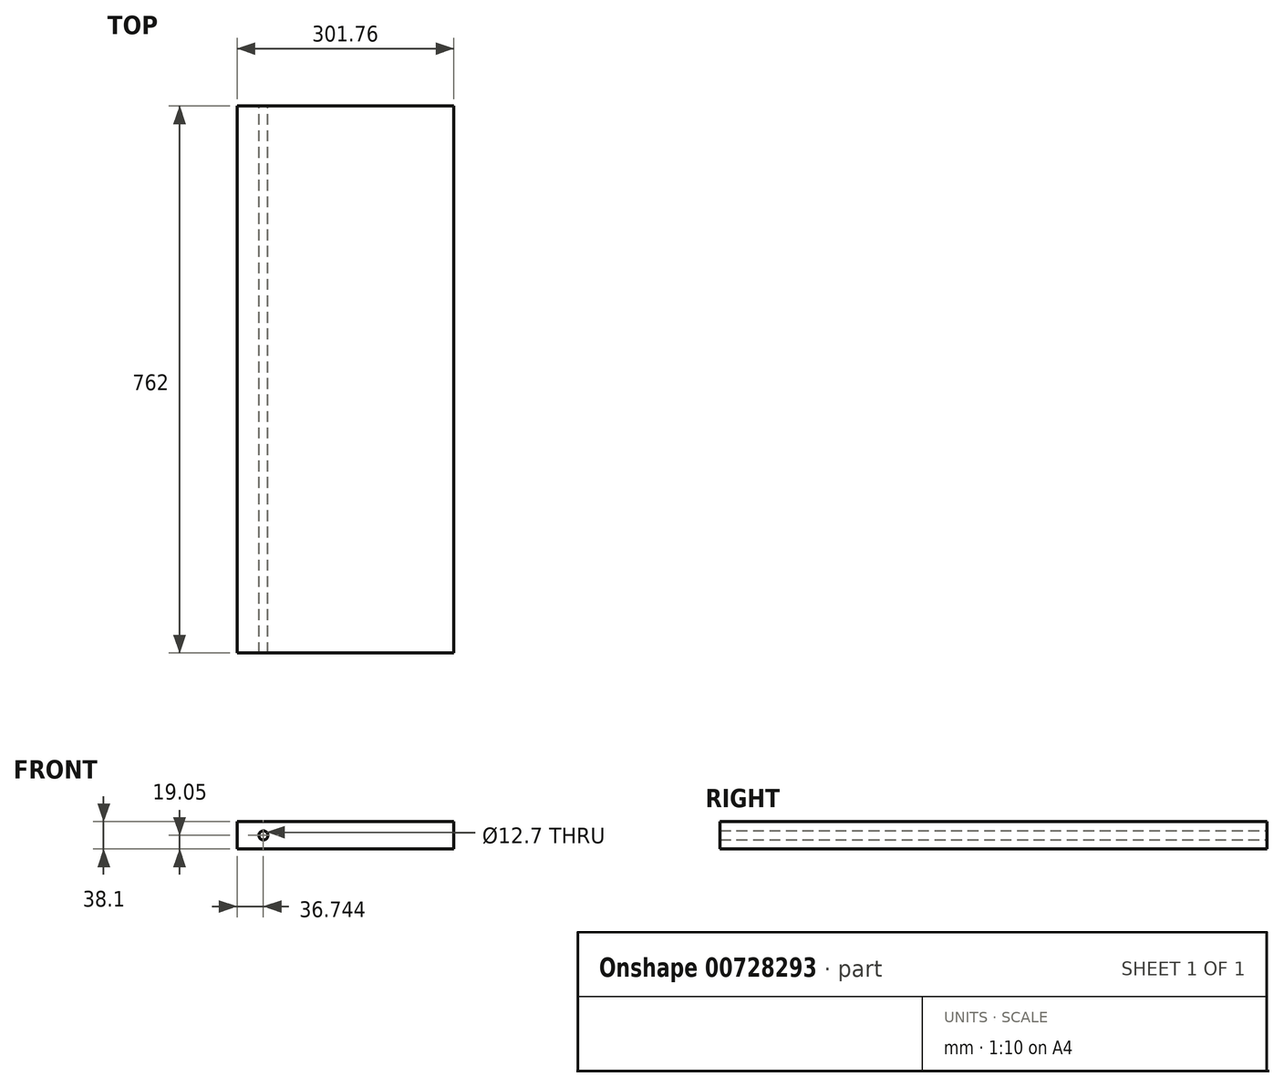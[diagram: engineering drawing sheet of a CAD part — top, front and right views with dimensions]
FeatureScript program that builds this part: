
annotation { "Feature Type Name" : "Feature", "Feature Type Description" : "" }
export const myFeature = defineFeature(function(context is Context, id is Id, definition is map)
    precondition{}
    {
        {
            var Q0;
            Q0=qCreatedBy(makeId("Front.planeOp"),FACE);
            var sketch = newSketch(context, id + "F0", { "sketchPlane" : qUnion([Q0])});
            skLineSegment(sketch, "E0.bottom", {"start": v(-150.88, -19.05) * mm, "end": v(150.88, -19.05) * mm});
            skLineSegment(sketch, "E0.top", {"start": v(-150.88, 19.05) * mm, "end": v(150.88, 19.05) * mm});
            skLineSegment(sketch, "E0.left", {"start": v(-150.88, -19.05) * mm, "end": v(-150.88, 19.05) * mm});
            skLineSegment(sketch, "E0.right", {"start": v(150.88, -19.05) * mm, "end": v(150.88, 19.05) * mm});
            skPoint(sketch, "E0.middle", {"position": v(0, 0) * mm});
            skCircle(sketch, "E1", {"center": v(-114.14, 0) * mm, "radius": 6.35 * mm});
            skSolve(sketch);
        }
        {
            var Q0;
            Q0=qSketchRegion(id+"F0",true);
            extrude(context, id + "F1", {"entities" : qUnion([Q0]), "depth" : 762 * mm, "offsetDistance" : 25.4 * mm});
        }
    });
